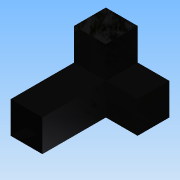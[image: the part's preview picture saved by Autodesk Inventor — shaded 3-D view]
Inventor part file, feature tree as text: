
AUTODESK INVENTOR PART (.ipt)
format: ipt  version: 2015 (Build 190159000, 159)  size: 98,816 bytes
history: native  units: in
note: dims shown in document units (in); Inventor stores cm internally (conversion verified against a paired STEP export)
features: extrude x2, sketch x2
ambient origin geometry x8: Origin, YZ Plane, XZ Plane, XY Plane, X Axis, Y Axis, Z Axis, Center Point
bodies: Solid1 (feature_tree)
feature tree (4):
  extrude  "Extrusion1"  Depth=2.0in
  extrude  "Extrusion2"  Depth=1.0in
  sketch  "Sketch1"  dims[d0=3.0in d1=2.0in]
  sketch  "Sketch2"  dims[d4=1.0in d5=0.0in d6=1.0in d7=1.0in d8=1.0in d9=1.0in d10=0.0in d11=1.0in d12=2.0in d13=1.0in]
